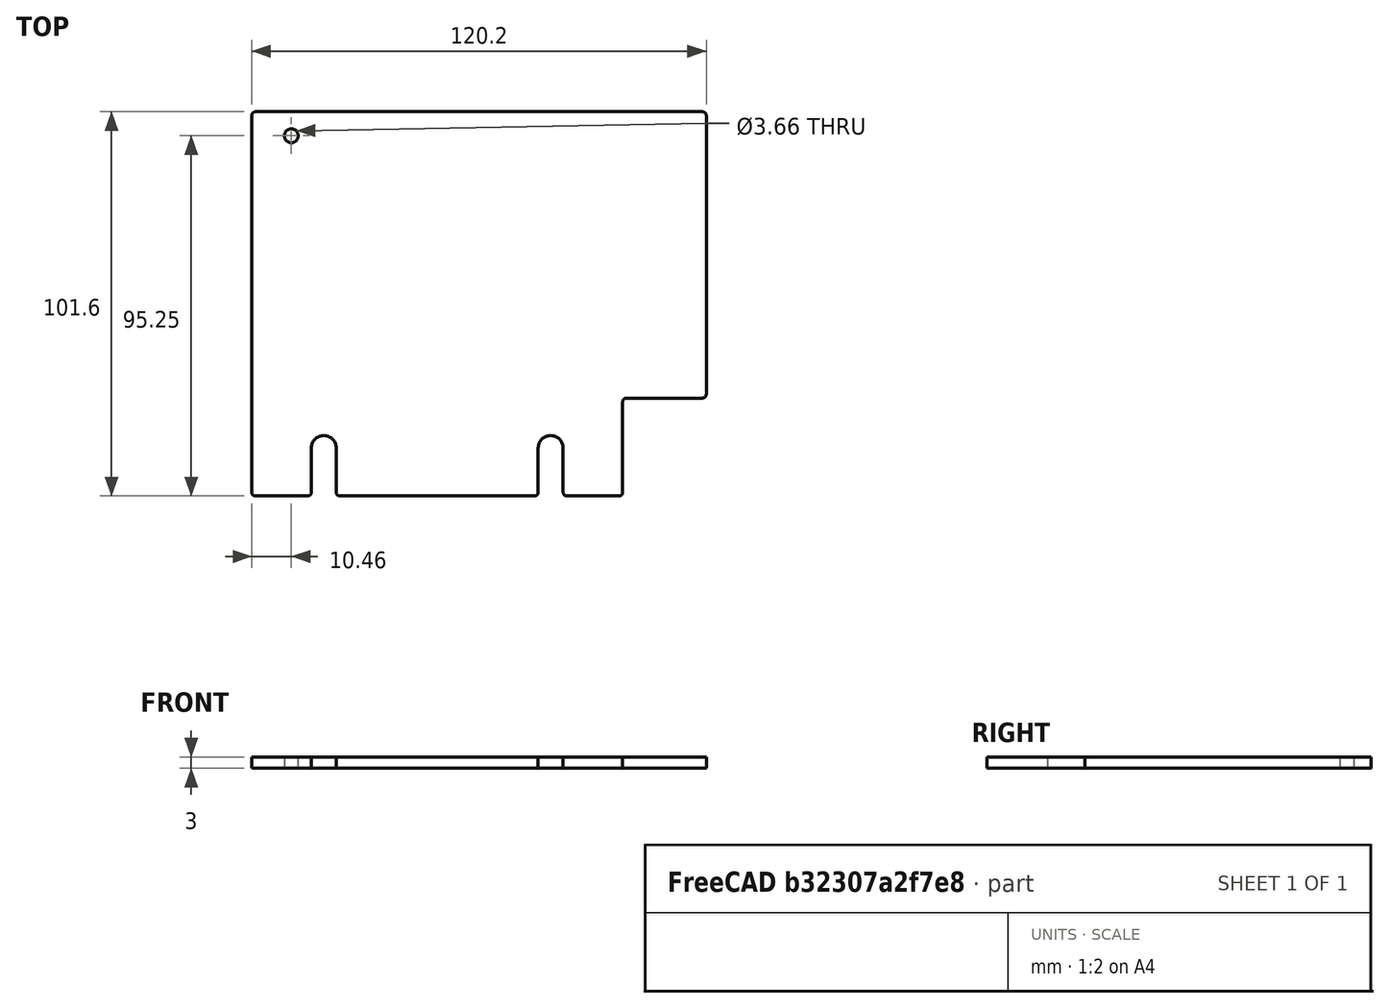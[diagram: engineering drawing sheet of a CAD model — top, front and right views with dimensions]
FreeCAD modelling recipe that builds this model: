
FCSTD DOCUMENT  (FreeCAD 0.21R33675 (Git))
Label: right_wall_back
License: All rights reserved
LicenseURL: http://en.wikipedia.org/wiki/All_rights_reserved
objects: Spreadsheet::Sheet×1, Sketcher::SketchObject×1, PartDesign::Pad×1, PartDesign::Body×1
note: 4 computed .brp shape members not serialized (recipe doc carries the construction recipe); baked Part::Feature solids carry a one-line shape summary decoded from their .brp

FEATURE [Spreadsheet::Sheet] Spreadsheet
  cells = A2='Parameters; A3='ServoOffsetFromCenter; B3(ServoOffsetFromCenter)==-3 in; A4='BeamLength; B4(BeamLength)==18 in; A5='BracketLength; B5(BracketLength)==108.6 mm; A6='DistanceLeftBracketEdgeToDoor; B6(DistanceLeftBracketEdgeToDoor)==82.4999 mm; A7='DistanceRightBracketEdgeToDoor; B7(DistanceRightBracketEdgeToDoor)==23.1001 mm; A8='DoorMargin; B8(DoorMargin)==1 mm; A9='LengthMargin; B9(LengthMargin)==0 mm; A10='LengthLeftBracketEdgeToDoorGap; B10(LengthLeftBracketEdgeToDoorGap)==DistanceLeftBracketEdgeToDoor - DoorMargin; A11='LengthRightBracketEdgeToDoorGap; B11(LengthRightBracketEdgeToDoorGap)==DistanceRightBracketEdgeToDoor - DoorMargin; A12='LengthDoorGap; B12(LengthDoorGap)==BracketLength - LengthLeftBracketEdgeToDoorGap - LengthRightBracketEdgeToDoorGap; A13='BeamLengthMinusBracketLength; B13(BeamLengthMinusBracketLength)==BeamLength - BracketLength; A14='DistanceBackToDoor; B14(DistanceBackToDoor)==0.5 * BeamLengthMinusBracketLength + LengthRightBracketEdgeToDoorGap + ServoOffsetFromCenter; A15='DistanceBackToBracket; B15(DistanceBackToBracket)==0.5 * BeamLengthMinusBracketLength + ServoOffsetFromCenter; A16='LengthBackToDoor; B16(LengthBackToDoor)==DistanceBackToDoor - LengthMargin; A17='LengthBackToBracket; B17(LengthBackToBracket)==DistanceBackToBracket - LengthMargin; A18='Height; B18(Height)==4 in; A19='Thickness; B19(Thickness)==3 mm; A20='CutoutMargin; B20(CutoutMargin)==0.5 mm; A21='CutoutHeight; B21(CutoutHeight)==1 in + CutoutMargin; A22='FilletRadius; B22(FilletRadius)==1 mm; A23='MountHoleDiameter; B23(MountHoleDiameter)==0.26 in; A24='MountHoleDistanceFromBottom; B24(MountHoleDistanceFromBottom)==0.5 in; A25='MountHoleSideMargin; B25(MountHoleSideMargin)==0.75 in; A27='RABracketWidth; B27(RABracketWidth)==0.5 in; A28='RABracketHoleDiameter; B28(RABracketHoleDiameter)==0.144 in; A29='RABracketHoleOffset; B29(RABracketHoleOffset)==0.412 in; A30='RAUpperBracketHoleFromTop; B30(RAUpperBracketHoleFromTop)==0.5 * RABracketWidth; A31='RABracketHoleFromSide; B31(RABracketHoleFromSide)==RABracketHoleOffset
FEATURE [Sketcher::SketchObject] Sketch
  FullyConstrained = true
  MapMode = 5
  Support = -> [XY_Plane]
  expr: Constraints[103] = Spreadsheet.RAUpperBracketHoleFromTop
  expr: Constraints[105] = Spreadsheet.RABracketHoleDiameter
  expr: Constraints[14] = Spreadsheet.FilletRadius
  expr: Constraints[20] = Spreadsheet.Height
  expr: Constraints[43] = Spreadsheet.MountHoleDistanceFromBottom
  expr: Constraints[44] = Spreadsheet.MountHoleDiameter
  expr: Constraints[59] = Spreadsheet.MountHoleSideMargin
  expr: Constraints[7] = Spreadsheet.LengthBackToDoor
  expr: Constraints[8] = Spreadsheet.LengthBackToBracket
  expr: Constraints[9] = Spreadsheet.CutoutHeight
  sketch-geometry (43):
    g0: LineSegment StartX=0 StartY=100.6 StartZ=0 EndX=0 EndY=1 EndZ=0
    g1: LineSegment StartX=1 StartY=0 StartZ=0 EndX=97.1 EndY=0 EndZ=0
    g2: LineSegment StartX=98.1 StartY=1 StartZ=0 EndX=98.1 EndY=24.9 EndZ=0
    g3: LineSegment StartX=99.1 StartY=25.9 StartZ=0 EndX=119.2 EndY=25.9 EndZ=0
    g4: LineSegment StartX=120.2 StartY=26.9 StartZ=0 EndX=120.2 EndY=100.6 EndZ=0
    g5: LineSegment StartX=119.2 StartY=101.6 StartZ=0 EndX=1 EndY=101.6 EndZ=0
    g6: ArcOfCircle CenterX=1 CenterY=100.6 CenterZ=0 NormalX=0 NormalY=0 NormalZ=1 AngleXU=0 Radius=1 StartAngle=1.5708 EndAngle=3.14159
    g7: GeomPoint X=0 Y=101.6 Z=0
    g8: ArcOfCircle CenterX=1 CenterY=1 CenterZ=0 NormalX=0 NormalY=0 NormalZ=1 AngleXU=0 Radius=1 StartAngle=3.14159 EndAngle=4.71239
    g9: GeomPoint X=0 Y=0 Z=0
    g10: ArcOfCircle CenterX=97.1 CenterY=1 CenterZ=0 NormalX=0 NormalY=0 NormalZ=1 AngleXU=0 Radius=1 StartAngle=4.71239 EndAngle=6.28319
    g11: GeomPoint X=98.1 Y=0 Z=0
    g12: ArcOfCircle CenterX=99.1 CenterY=24.9 CenterZ=0 NormalX=0 NormalY=0 NormalZ=1 AngleXU=0 Radius=1 StartAngle=1.5708 EndAngle=3.14159
    g13: GeomPoint X=98.1 Y=25.9 Z=0
    g14: ArcOfCircle CenterX=119.2 CenterY=26.9 CenterZ=0 NormalX=0 NormalY=0 NormalZ=1 AngleXU=0 Radius=1 StartAngle=4.71239 EndAngle=6.28319
    g15: GeomPoint X=120.2 Y=25.9 Z=0
    g16: ArcOfCircle CenterX=119.2 CenterY=100.6 CenterZ=0 NormalX=0 NormalY=0 NormalZ=1 AngleXU=0 Radius=1 StartAngle=4.1e-15 EndAngle=1.5708
    g17: GeomPoint X=120.2 Y=101.6 Z=0
    g18: GeomPoint X=19.05 Y=0 Z=0
    g19: LineSegment StartX=19.05 StartY=0 StartZ=0 EndX=19.05 EndY=12.7 EndZ=0
    g20: Circle CenterX=19.05 CenterY=12.7 CenterZ=0 NormalX=0 NormalY=0 NormalZ=1 AngleXU=0 Radius=3.302
    g21: LineSegment StartX=79.05 StartY=12.7 StartZ=0 EndX=79.05 EndY=0 EndZ=0
    g22: LineSegment StartX=79.05 StartY=12.7 StartZ=0 EndX=98.1 EndY=12.7 EndZ=0
    g23: LineSegment StartX=19.05 StartY=12.7 StartZ=0 EndX=0 EndY=12.7 EndZ=0
    g24: Circle CenterX=79.05 CenterY=12.7 CenterZ=0 NormalX=0 NormalY=0 NormalZ=1 AngleXU=0 Radius=3.302
    g25: ArcOfCircle CenterX=19.05 CenterY=12.7 CenterZ=0 NormalX=0 NormalY=0 NormalZ=1 AngleXU=0 Radius=3.302 StartAngle=0 EndAngle=3.14159
    g26: LineSegment StartX=19.05 StartY=12.7 StartZ=0 EndX=22.352 EndY=12.7 EndZ=0
    g27: LineSegment StartX=15.748 StartY=12.7 StartZ=0 EndX=15.748 EndY=1 EndZ=0
    g28: LineSegment StartX=22.352 StartY=12.7 StartZ=0 EndX=22.352 EndY=1 EndZ=0
    g29: ArcOfCircle CenterX=14.748 CenterY=1 CenterZ=0 NormalX=0 NormalY=0 NormalZ=1 AngleXU=0 Radius=1 StartAngle=4.71239 EndAngle=6.28319
    g30: ArcOfCircle CenterX=23.352 CenterY=1 CenterZ=0 NormalX=0 NormalY=0 NormalZ=1 AngleXU=0 Radius=1 StartAngle=3.14159 EndAngle=4.71239
    g31: ArcOfCircle CenterX=79.05 CenterY=12.7 CenterZ=0 NormalX=0 NormalY=0 NormalZ=1 AngleXU=0 Radius=3.302 StartAngle=-2.7e-15 EndAngle=3.14159
    g32: LineSegment StartX=79.05 StartY=12.7 StartZ=0 EndX=75.748 EndY=12.7 EndZ=0
    g33: LineSegment StartX=75.748 StartY=12.7 StartZ=0 EndX=75.748 EndY=1 EndZ=0
    g34: LineSegment StartX=82.352 StartY=12.7 StartZ=0 EndX=82.352 EndY=1 EndZ=0
    g35: ArcOfCircle CenterX=74.748 CenterY=1 CenterZ=0 NormalX=0 NormalY=0 NormalZ=1 AngleXU=0 Radius=1 StartAngle=4.71239 EndAngle=6.28319
    g36: ArcOfCircle CenterX=83.352 CenterY=1 CenterZ=0 NormalX=0 NormalY=0 NormalZ=1 AngleXU=0 Radius=1 StartAngle=3.14159 EndAngle=4.71239
    g37: LineSegment StartX=83.352 StartY=0 StartZ=0 EndX=97.1 EndY=0 EndZ=0
    g38: LineSegment StartX=23.352 StartY=0 StartZ=0 EndX=74.748 EndY=0 EndZ=0
    g39: LineSegment StartX=1 StartY=0 StartZ=0 EndX=14.748 EndY=0 EndZ=0
    g40: LineSegment StartX=0 StartY=101.6 StartZ=0 EndX=10.46 EndY=101.6 EndZ=0
    g41: LineSegment StartX=10.46 StartY=101.6 StartZ=0 EndX=10.46 EndY=95.25 EndZ=0
    g42: Circle CenterX=10.46 CenterY=95.25 CenterZ=0 NormalX=0 NormalY=0 NormalZ=1 AngleXU=0 Radius=1.8288
  constraints (106):
    c: Vertical(g0)
    c: Horizontal(g1)
    c: Vertical(g2)
    c: Horizontal(g3)
    c: Vertical(g4)
    c: Horizontal(g5)
    c: Coincident(g-1,g9)
    c: DistanceX(g7,g17) = 120.2
    c: DistanceX(g9,g11) = 98.1
    c: DistanceY(g11,g13) = 25.9
    c: PointOnObject(g7,g0)
    c: PointOnObject(g7,g5)
    c: Tangent(g0,g6) = -1.5708
    c: Tangent(g5,g6) = -1.5708
    c: Radius(g6) = 1
    c: PointOnObject(g9,g0)
    c: PointOnObject(g9,g1)
    c: Tangent(g0,g8) = -1.5708
    c: Tangent(g1,g8) = -1.5708
    c: Equal(g8,g6)
    c: DistanceY(g1,g5) = 101.6
    c: PointOnObject(g11,g1)
    c: PointOnObject(g11,g2)
    c: Tangent(g1,g10) = -1.5708
    c: Tangent(g2,g10) = -1.5708
    c: Equal(g10,g8)
    c: PointOnObject(g13,g2)
    c: PointOnObject(g13,g3)
    c: Tangent(g2,g12) = 1.5708
    c: Tangent(g3,g12) = 1.5708
    c: Equal(g12,g10)
    c: PointOnObject(g15,g3)
    c: PointOnObject(g15,g4)
    c: Tangent(g3,g14) = -1.5708
    c: Tangent(g4,g14) = -1.5708
    c: Equal(g14,g12)
    c: PointOnObject(g17,g5)
    c: PointOnObject(g17,g4)
    c: Tangent(g5,g16) = -1.5708
    c: Tangent(g4,g16) = -1.5708
    c: Equal(g16,g14)
    c: Coincident(g19,g18)
    c: Vertical(g19)
    c: DistanceY(g19,g19) = 12.7
    c: Diameter(g20) = 6.604
    c: Coincident(g20,g19)
    c: PointOnObject(g18,g1)
    c: PointOnObject(g21,g1)
    c: Vertical(g21)
    c: Equal(g19,g21)
    c: Coincident(g22,g21)
    c: PointOnObject(g22,g2)
    c: Horizontal(g22)
    c: Coincident(g23,g20)
    c: PointOnObject(g23,g0)
    c: Horizontal(g23)
    c: Equal(g23,g22)
    c: Coincident(g24,g21)
    c: Equal(g24,g20)
    c: DistanceX(g23,g23) = 19.05
    c: Coincident(g25,g19)
    c: PointOnObject(g25,g23)
    c: Coincident(g26,g25)
    c: Coincident(g26,g25)
    c: Horizontal(g26)
    c: PointOnObject(g25,g20)
    c: Coincident(g27,g25)
    c: Vertical(g27)
    c: Coincident(g28,g25)
    c: Vertical(g28)
    c: Equal(g27,g28)
    c: Tangent(g29,g27) = 1.5708
    c: Tangent(g29,g1) = -1.5708
    c: Tangent(g30,g28) = -1.5708
    c: Tangent(g30,g1) = -1.5708
    c: Equal(g29,g8)
    c: Coincident(g31,g21)
    c: PointOnObject(g31,g22)
    c: Coincident(g32,g31)
    c: Coincident(g32,g31)
    c: Horizontal(g32)
    c: PointOnObject(g31,g24)
    c: Coincident(g33,g31)
    c: Vertical(g33)
    c: Coincident(g34,g31)
    c: Vertical(g34)
    c: Equal(g33,g34)
    c: Tangent(g35,g33) = 1.5708
    c: Tangent(g35,g1) = -1.5708
    c: Tangent(g36,g34) = -1.5708
    c: Tangent(g36,g1) = -1.5708
    c: Equal(g36,g10)
    c: Coincident(g37,g36)
    c: Coincident(g37,g10)
    c: Coincident(g38,g30)
    c: Coincident(g38,g35)
    c: Coincident(g39,g8)
    c: Coincident(g39,g29)
    c: Horizontal(g40)
    c: Coincident(g7,g40)
    c: DistanceX(g40,g40) = 10.46
    c: Coincident(g41,g40)
    c: Vertical(g41)
    c: DistanceY(g41,g41) = 6.35
    c: Coincident(g42,g41)
    c: Diameter(g42) = 3.6576
FEATURE [PartDesign::Pad] Pad
  Direction = (0,0,1)
  Length = 3
  Length2 = 10
  Profile = -> Sketch
  ReferenceAxis = -> Sketch [N_Axis]
  Type = 0
  expr: Length = Spreadsheet.Thickness
FEATURE [PartDesign::Body] Body
  Group = -> [Sketch,Pad]
  Origin = -> Origin
  Tip = -> Pad
